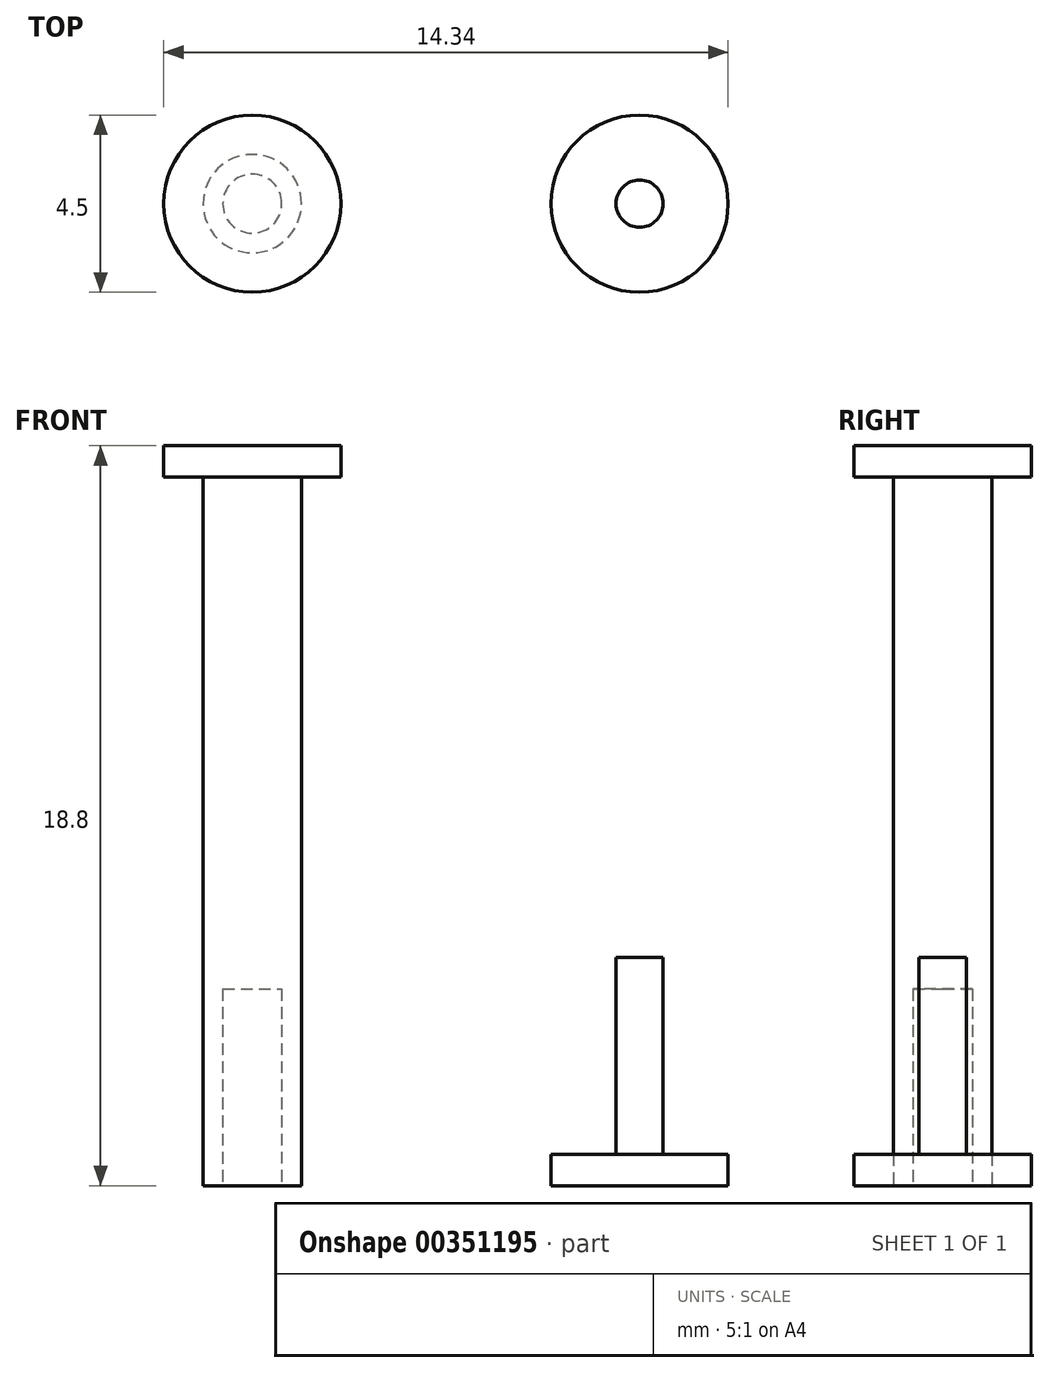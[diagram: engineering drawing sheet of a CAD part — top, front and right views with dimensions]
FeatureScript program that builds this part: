
annotation { "Feature Type Name" : "Feature", "Feature Type Description" : "" }
export const myFeature = defineFeature(function(context is Context, id is Id, definition is map)
    precondition{}
    {
        {
            var Q0;
            Q0=qCreatedBy(makeId("Top.planeOp"),FACE);
            var sketch = newSketch(context, id + "F0", { "sketchPlane" : qUnion([Q0])});
            skCircle(sketch, "E0", {"center": v(0, 0) * mm, "radius": 1.25 * mm});
            skSolve(sketch);
        }
        {
            var Q0;
            Q0=makeQuery(id+"F0.imprint","IMPRINT",FACE,{"disambiguationData":[TD([[makeQuery(id+"F0.imprint","IMPRINT",EDGE,{"derivedFrom":sQuery(id+"F0.wireOp",EDGE,"E0")}),1.0]])]});
            extrude(context, id + "F1", {"entities" : qUnion([Q0]), "depth" : 18 * mm});
        }
        {
            var Q0;
            Q0=makeQuery(id+"F1.opExtrude","CAP_FACE",FACE,{"disambiguationData":[OSD([sQuery(id+"F0.wireOp",EDGE,"E0")])],"isStart":false});
            var sketch = newSketch(context, id + "F2", { "sketchPlane" : qUnion([Q0])});
            skCircle(sketch, "E1", {"center": v(0, 0) * mm, "radius": 2.25 * mm});
            skLineSegment(sketch, "E2", {"start": v(0, 1.25) * mm, "end": v(0, -1.25) * mm});
            skSolve(sketch);
        }
        {
            var Q0;
            {var subQ0=sQuery(id+"F2.wireOp",EDGE,"E2");Q0=makeQuery(id+"F2.imprint","IMPRINT",FACE,{"disambiguationData":[TD([[makeQuery(id+"F2.imprint","IMPRINT",EDGE,{"derivedFrom":subQ0}),1.0]])]});}
            var Q1;
            {var subQ0=sQuery(id+"F2.wireOp",EDGE,"E2");Q1=makeQuery(id+"F2.imprint","IMPRINT",FACE,{"disambiguationData":[TD([[makeQuery(id+"F2.imprint","IMPRINT",EDGE,{"derivedFrom":subQ0}),-1.0]])]});}
            var Q2;
            Q2=makeQuery(id+"F2.imprint","IMPRINT",FACE,{"disambiguationData":[TD([[makeQuery(id+"F2.imprint","IMPRINT",EDGE,{"derivedFrom":sQuery(id+"F2.wireOp",EDGE,"E1")}),1.0]])]});
            extrude(context, id + "F3", {"entities" : qUnion([Q0, Q1, Q2]), "operationType" : NewBodyOperationType.ADD, "depth" : 0.8 * mm});
        }
        {
            var Q0;
            Q0=makeQuery(id+"F1.opExtrude","CAP_FACE",FACE,{"disambiguationData":[OSD([sQuery(id+"F0.wireOp",EDGE,"E0")])],"isStart":true});
            var sketch = newSketch(context, id + "F4", { "sketchPlane" : qUnion([Q0])});
            skSolve(sketch);
        }
        {
            var Q0;
            Q0=makeQuery(id+"F4.imprint","IMPRINT",FACE,{"disambiguationData":[TD([[makeQuery(id+"F4.imprint","IMPRINT",EDGE,{"derivedFrom":makeQuery(id+"F1.opExtrude","CAP_EDGE",EDGE,{"disambiguationData":[OSD([sQuery(id+"F0.wireOp",EDGE,"E0")])],"isStart":true})}),-1.0]])]});
            var sketch = newSketch(context, id + "F5", { "sketchPlane" : qUnion([Q0])});
            skCircle(sketch, "E3", {"center": v(0, 0) * mm, "radius": 0.75 * mm});
            skSolve(sketch);
        }
        {
            var Q0;
            Q0=makeQuery(id+"F5.imprint","IMPRINT",FACE,{"disambiguationData":[TD([[makeQuery(id+"F5.imprint","IMPRINT",EDGE,{"derivedFrom":sQuery(id+"F5.wireOp",EDGE,"E3")}),1.0]])]});
            extrude(context, id + "F6", {"entities" : qUnion([Q0]), "operationType" : NewBodyOperationType.REMOVE, "oppositeDirection" : true, "depth" : 5 * mm});
        }
        {
            var Q0;
            Q0=qCreatedBy(makeId("Top.planeOp"),FACE);
            var sketch = newSketch(context, id + "F7", { "sketchPlane" : qUnion([Q0])});
            skCircle(sketch, "E4", {"center": v(9.84, 0) * mm, "radius": 2.25 * mm});
            skSolve(sketch);
        }
        {
            var Q0;
            Q0=makeQuery(id+"F7.imprint","IMPRINT",FACE,{"disambiguationData":[TD([[makeQuery(id+"F7.imprint","IMPRINT",EDGE,{"derivedFrom":sQuery(id+"F7.wireOp",EDGE,"E4")}),1.0]])]});
            extrude(context, id + "F8", {"entities" : qUnion([Q0]), "depth" : 0.8 * mm});
        }
        {
            var Q0;
            Q0=makeQuery(id+"F8.opExtrude","CAP_FACE",FACE,{"disambiguationData":[OSD([sQuery(id+"F7.wireOp",EDGE,"E4")])],"isStart":false});
            var sketch = newSketch(context, id + "F9", { "sketchPlane" : qUnion([Q0])});
            skCircle(sketch, "E5", {"center": v(9.84, 0) * mm, "radius": 0.6 * mm});
            skSolve(sketch);
        }
        {
            var Q0;
            Q0=makeQuery(id+"F9.imprint","IMPRINT",FACE,{"disambiguationData":[TD([[makeQuery(id+"F9.imprint","IMPRINT",EDGE,{"derivedFrom":sQuery(id+"F9.wireOp",EDGE,"E5")}),1.0]])]});
            extrude(context, id + "F10", {"entities" : qUnion([Q0]), "operationType" : NewBodyOperationType.ADD, "depth" : 5 * mm});
        }
    });
